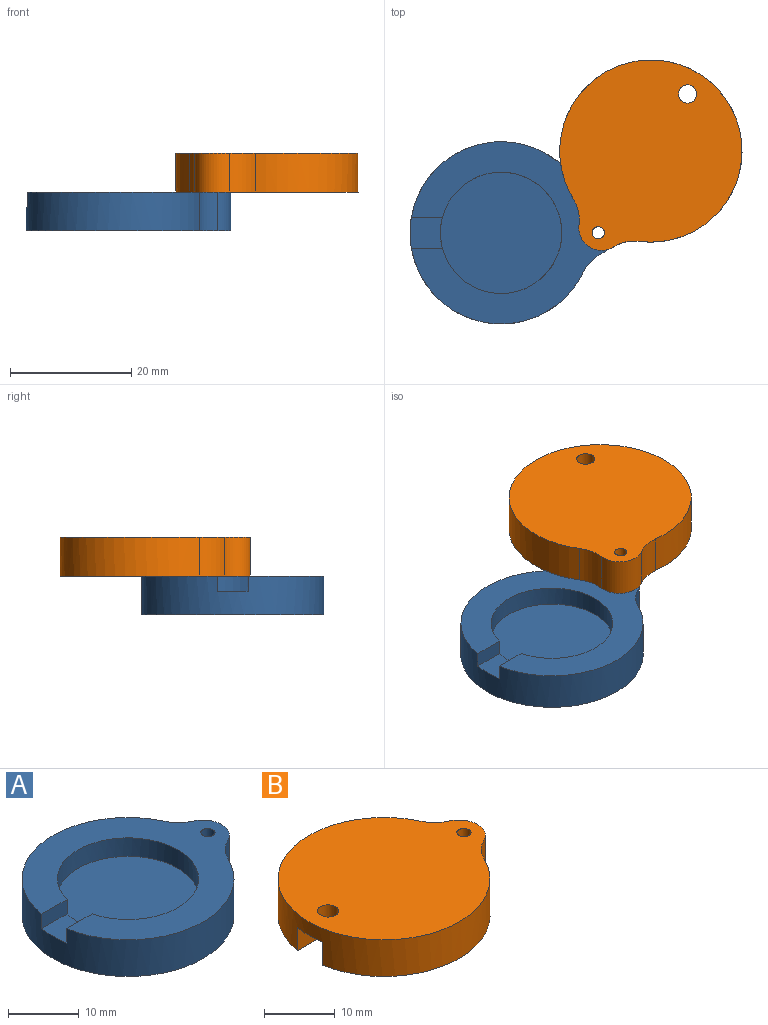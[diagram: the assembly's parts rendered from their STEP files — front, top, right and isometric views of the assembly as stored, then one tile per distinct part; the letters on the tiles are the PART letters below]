
ASSEMBLY  parts=2 mates=1
PART A: 12 faces, bbox 33.8x30x6.4 mm
  f0: cylinder r=15mm len=30mm, axis (0,0,1), area 501.6mm2, adj f1,f4,f6,f7,f8,f9,f10
  f1: plane 33.54x30mm, normal (0,0,1), area 390.1mm2, adj f0,f2,f3,f6,f7,f8,f9,f11
  f2: cylinder r=10mm len=20mm, axis (0,0,1), area 188.4mm2, adj f1,f5,f8,f9,f10
  f3: cylinder r=3.75mm len=6.79mm, axis (0,0,1), area 53.9mm2, adj f1,f4,f6,f7
  f4: plane 33.75x30mm, normal (0,0,-1), area 729.4mm2, adj f0,f3,f6,f7,f11
  f5: plane 20x20mm, normal (0,0,1), area 314.2mm2, adj f2
  f6: cylinder r=6.35mm len=6.35mm, axis (0,0,-1), area 27.8mm2, adj f0,f1,f3,f4
  f7: cylinder r=6.35mm len=6.35mm, axis (0,0,-1), area 27.8mm2, adj f0,f1,f3,f4
  f8: plane 5.11x2.5mm, normal (0,-1,0), area 12.8mm2, adj f0,f1,f2,f10
  f9: plane 5.11x2.5mm, normal (0,1,0), area 12.8mm2, adj f0,f1,f2,f10
  f10: plane 5.32x5mm, normal (0,0,1), area 25.2mm2, adj f0,f2,f8,f9
  f11: cylinder r=1mm len=6.35mm, axis (0,0,1), area 39.9mm2, adj f1,f4
PART B: 14 faces, bbox 33.8x30x6.4 mm
  f0: plane 33.54x30mm, normal (0,0,-1), area 390.1mm2, adj f1,f2,f4,f6,f7,f9,f10,f12
  f1: cylinder r=15mm len=30mm, axis (0,0,-1), area 494.1mm2, adj f0,f3,f6,f7,f8,f9,f10
  f2: cylinder r=3.75mm len=6.79mm, axis (0,0,-1), area 53.9mm2, adj f0,f3,f6,f7
  f3: plane 33.75x30mm, normal (0,0,1), area 722.3mm2, adj f1,f2,f6,f7,f12,f13
  f4: cylinder r=10mm len=20mm, axis (0,0,-1), area 57.8mm2, adj f0,f5,f9,f10
  f5: plane 20x19.68mm, normal (0,0,-1), area 297.4mm2, adj f4,f9,f10,f11
  f6: cylinder r=6.35mm len=6.35mm, axis (0,0,1), area 27.8mm2, adj f0,f1,f2,f3
  f7: cylinder r=6.35mm len=6.35mm, axis (0,0,1), area 27.8mm2, adj f0,f1,f2,f3
  f8: plane 8.45x5mm, normal (0,0,-1), area 34.8mm2, adj f1,f9,f10,f11,f13
  f9: plane 8.24x4mm, normal (0,-1,0), area 29.8mm2, adj f0,f1,f4,f5,f8,f11
  f10: plane 8.24x4mm, normal (0,1,0), area 29.8mm2, adj f0,f1,f4,f5,f8,f11
  f11: plane 5x3mm, normal (-1,0,0), area 15mm2, adj f5,f8,f9,f10
  f12: cylinder r=1mm len=6.35mm, axis (0,0,-1), area 39.9mm2, adj f0,f3
  f13: cylinder r=1.5mm len=3mm, axis (0,0,1), area 22.1mm2, adj f3,f8
PLACE A at identity fixed
PLACE B rot(axis=(0,0,-1),122.8deg) t=(24.66,13.45,0)mm
MATE revolute B.f12 <-> A.f11  axis (0,0,-1) through (16,0,0)mm
